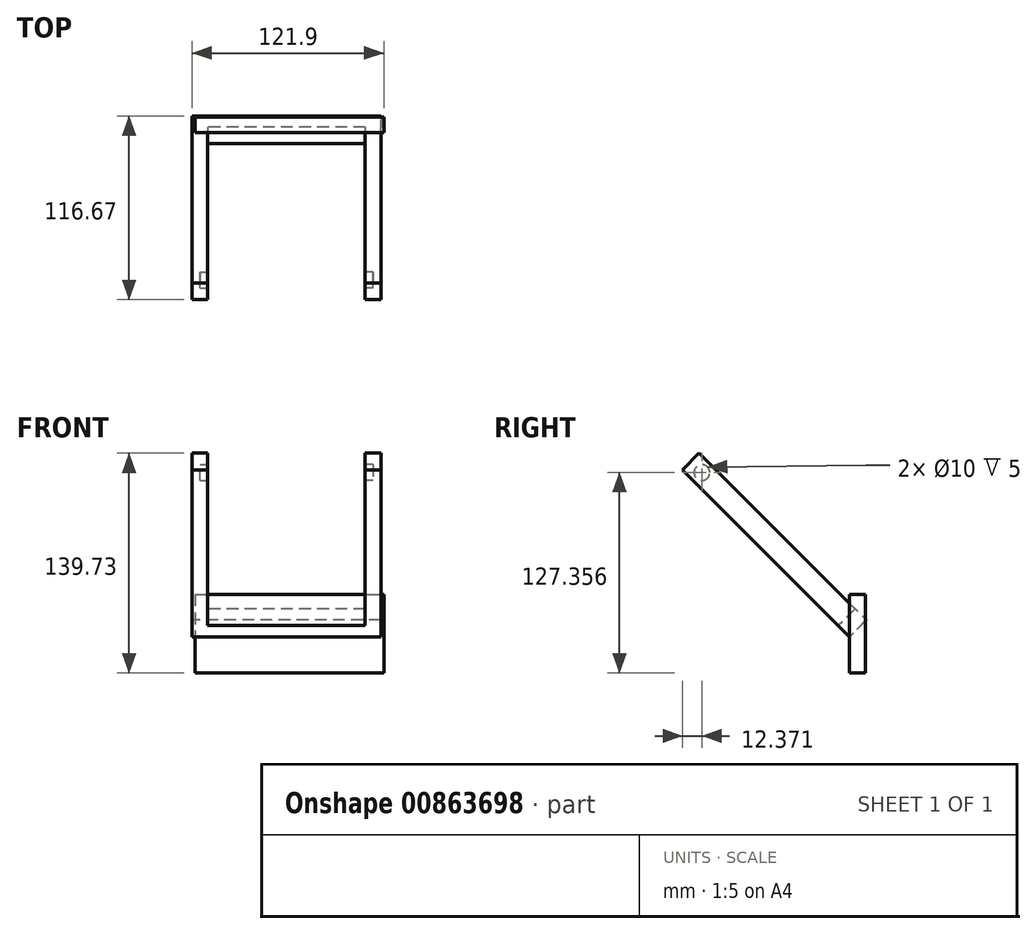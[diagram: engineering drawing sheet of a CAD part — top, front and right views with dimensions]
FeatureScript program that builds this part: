
annotation { "Feature Type Name" : "Feature", "Feature Type Description" : "" }
export const myFeature = defineFeature(function(context is Context, id is Id, definition is map)
    precondition{}
    {
        {
            var Q0;
            Q0=qCreatedBy(makeId("Top.planeOp"),FACE);
            var sketch = newSketch(context, id + "F0", { "sketchPlane" : qUnion([Q0])});
            skLineSegment(sketch, "E0", {"start": v(-59.02, 0) * mm, "end": v(58.14, 0) * mm});
            skSolve(sketch);
        }
        {
            var Q0;
            Q0=sQuery(id+"F0.wireOp",EDGE,"E0");
            cPlane(context, id + "F1", {"entities" : qUnion([Q0]), "cplaneType" : CPlaneType.LINE_ANGLE, "offset" : 25 * mm, "angle" : 45 * degree, "width" : 150 * mm, "height" : 150 * mm});
        }
        {
            var Q0;
            Q0=qCreatedBy(id+"F1.planeOp",FACE);
            var sketch = newSketch(context, id + "F2", { "sketchPlane" : qUnion([Q0])});
            skLineSegment(sketch, "E1", {"start": v(-35.76, 101.09) * mm, "end": v(-35.76, -33.91) * mm});
            skLineSegment(sketch, "E2", {"start": v(-35.76, -33.91) * mm, "end": v(64.24, -33.91) * mm});
            skLineSegment(sketch, "E3", {"start": v(64.24, -33.91) * mm, "end": v(64.24, 101.09) * mm});
            skLineSegment(sketch, "E4.0", {"start": v(-45.76, 106.09) * mm, "end": v(-45.76, -43.91) * mm});
            skLineSegment(sketch, "E5.0", {"start": v(-45.76, -43.91) * mm, "end": v(74.24, -43.91) * mm});
            skLineSegment(sketch, "E6.0", {"start": v(74.24, -43.91) * mm, "end": v(74.24, 106.09) * mm});
            skLineSegment(sketch, "E7", {"start": v(-35.76, 106.09) * mm, "end": v(-45.76, 106.09) * mm});
            skLineSegment(sketch, "E8", {"start": v(64.24, 106.09) * mm, "end": v(74.24, 106.09) * mm});
            skLineSegment(sketch, "E9", {"start": v(-35.76, 101.09) * mm, "end": v(-35.76, 106.09) * mm});
            skLineSegment(sketch, "E10", {"start": v(64.24, 101.09) * mm, "end": v(64.24, 106.09) * mm});
            skSolve(sketch);
        }
        {
            var Q0;
            Q0=makeQuery(id+"F2.imprint","IMPRINT",FACE,{"disambiguationData":[TD([[makeQuery(id+"F2.imprint","IMPRINT",EDGE,{"derivedFrom":sQuery(id+"F2.wireOp",EDGE,"E1")}),-1.0]])]});
            extrude(context, id + "F3", {"entities" : qUnion([Q0]), "depth" : 15 * mm, "offsetDistance" : 25 * mm});
        }
        {
            var Q0;
            Q0=makeQuery(id+"F3.opExtrude","SWEPT_FACE",FACE,{"disambiguationData":[OSD([sQuery(id+"F2.wireOp",EDGE,"E3")])]});
            var sketch = newSketch(context, id + "F4", { "sketchPlane" : qUnion([Q0])});
            skCircle(sketch, "E11", {"center": v(-62.64, 73.25) * mm, "radius": 5 * mm});
            skSolve(sketch);
        }
        {
            var Q0;
            Q0=makeQuery(id+"F3.opExtrude","SWEPT_FACE",FACE,{"disambiguationData":[OSD([sQuery(id+"F2.wireOp",EDGE,"E1")])]});
            var sketch = newSketch(context, id + "F5", { "sketchPlane" : qUnion([Q0])});
            skCircle(sketch, "E12", {"center": v(62.64, 73.25) * mm, "radius": 5 * mm});
            skSolve(sketch);
        }
        {
            var Q0;
            Q0=makeQuery(id+"F4.imprint","IMPRINT",FACE,{"disambiguationData":[TD([[makeQuery(id+"F4.imprint","IMPRINT",EDGE,{"derivedFrom":sQuery(id+"F4.wireOp",EDGE,"E11")}),1.0]])]});
            var Q1;
            Q1=makeQuery(id+"F5.imprint","IMPRINT",FACE,{"disambiguationData":[TD([[makeQuery(id+"F5.imprint","IMPRINT",EDGE,{"derivedFrom":sQuery(id+"F5.wireOp",EDGE,"E12")}),1.0]])]});
            extrude(context, id + "F6", {"entities" : qUnion([Q0, Q1]), "operationType" : NewBodyOperationType.REMOVE, "oppositeDirection" : true, "depth" : 5 * mm, "offsetDistance" : 25 * mm});
        }
        {
            var Q0;
            Q0=makeQuery(id+"F5.imprint","IMPRINT",FACE,{"disambiguationData":[TD([[makeQuery(id+"F5.imprint","IMPRINT",EDGE,{"derivedFrom":sQuery(id+"F5.wireOp",EDGE,"E12")}),1.0]])]});
            extrude(context, id + "F7", {"entities" : qUnion([Q0]), "operationType" : NewBodyOperationType.REMOVE, "oppositeDirection" : true, "depth" : 5 * mm, "offsetDistance" : 25 * mm});
        }
        {
            var Q0;
            Q0=sQuery(id+"F2.wireOp",EDGE,"E5.0");
            cPlane(context, id + "F8", {"entities" : qUnion([Q0]), "cplaneType" : CPlaneType.LINE_ANGLE, "offset" : 25 * mm, "angle" : 0 * degree, "width" : 150 * mm, "height" : 150 * mm});
        }
        {
            var Q0;
            Q0=qCreatedBy(id+"F8.planeOp",FACE);
            var sketch = newSketch(context, id + "F9", { "sketchPlane" : qUnion([Q0])});
            skLineSegment(sketch, "E13.bottom", {"start": v(-72.34, -4.11) * mm, "end": v(47.66, -4.11) * mm});
            skLineSegment(sketch, "E13.top", {"start": v(-72.34, -54.11) * mm, "end": v(47.66, -54.11) * mm});
            skLineSegment(sketch, "E13.left", {"start": v(-72.34, -4.11) * mm, "end": v(-72.34, -54.11) * mm});
            skLineSegment(sketch, "E13.right", {"start": v(47.66, -4.11) * mm, "end": v(47.66, -54.11) * mm});
            skSolve(sketch);
        }
        {
            var Q0;
            Q0=makeQuery(id+"F9.imprint","IMPRINT",FACE,{"disambiguationData":[TD([[makeQuery(id+"F9.imprint","IMPRINT",EDGE,{"derivedFrom":sQuery(id+"F9.wireOp",EDGE,"E13.bottom")}),-1.0]])]});
            extrude(context, id + "F10", {"entities" : qUnion([Q0]), "oppositeDirection" : true, "depth" : 10 * mm, "offsetDistance" : 25 * mm});
        }
    });
